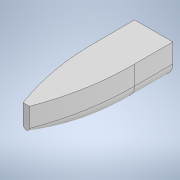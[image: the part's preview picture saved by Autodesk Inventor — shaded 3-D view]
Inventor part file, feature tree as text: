
AUTODESK INVENTOR PART (.ipt)
format: ipt  version: 2020.3 (Build 243373000, 373)  size: 196,608 bytes
history: native  units: mm
features: sketch x4, plane x4, extrude x1, loft x1, projected_geometry x1, other x1
ambient origin geometry x8: Origin, YZ Plane, XZ Plane, XY Plane, X Axis, Y Axis, Z Axis, Center Point
bodies: Solid1 (feature_tree)
feature tree (12):
  sketch  "Sketch1"  dims[d0=60.0mm d1=170.0mm]
  plane  "Work Plane1"
  plane  "Work Plane2"
  plane  "Work Plane3"
  plane  "Work Plane4"
  extrude  "Extrusion1"  Depth=170.0mm
  sketch  "Sketch2"  dims[d2=200.0mm d3=30.0mm]
  loft  "Loft3"
  projected_geometry  "Projected Loop1"
  sketch  "Sketch3"  dims[d4=60.0mm]
  sketch  "Sketch4"  dims[d5=30.0mm d7=18.0mm d8=30.0mm d9=18.0mm d10=30.0mm d11=10.0mm d12=0.0mm d13=30.0mm d14=15.126927mm d16=9.076156mm d17=15.0mm d18=15.0mm d19=9.076156mm d24=10.0mm d25=5.0mm d26=3.0mm d27=3.0mm d28=5.0mm d29=5.0mm d35=0.0mm d36=90.0deg d37=0.0mm d38=90.0deg d39=0.0mm d40=90.0deg]
  other  "Edges3"
